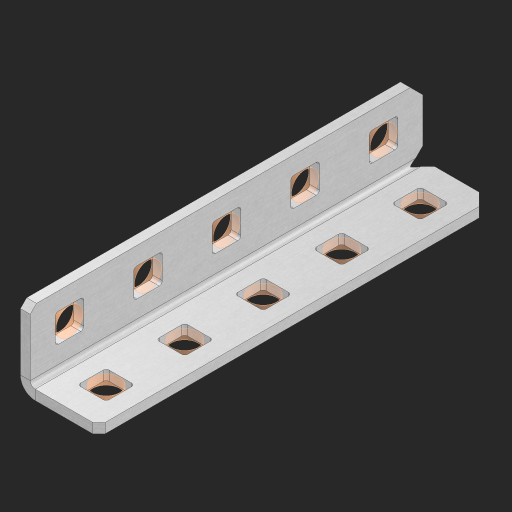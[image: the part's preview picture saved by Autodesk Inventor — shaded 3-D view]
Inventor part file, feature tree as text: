
AUTODESK INVENTOR PART (.ipt)
format: ipt  version: 2023 (Build 270158000, 158)  size: 510,976 bytes
history: native  units: in
note: dims shown in document units (in); Inventor stores cm internally (conversion verified against a paired STEP export)
features: other x16, extrude x11, sheet_metal_op x8, sketch x5, pattern_linear x1, mirror x1, chamfer x1
ambient origin geometry x8: Origin, YZ Plane, XZ Plane, XY Plane, X Axis, Y Axis, Z Axis, Center Point
bodies: Solid1 (feature_tree), Body (feature_tree)
feature tree (43):
  sheet_metal_op  "Flanges"
  sheet_metal_op  "Body Pattern"
  other  "Arc Length"
  pattern_linear  "Notch Pattern"  Spacing1=0.125in  [1 undecoded]
  other  "Diagonal Plane"
  mirror  "Everything Mirrored"
  chamfer  "End Chamfer"
  sketch  "Sketch1"  dims[d0=0.5in]
  other  "Plate1"
  sketch  "Sketch2"  dims[d1=2.5in]
  other  "Plate2"
  sheet_metal_op  "Bend1"
  sheet_metal_op  "Corner1"
  sketch  "Sketch8"  dims[d2=0.0625in]
  sketch  "Sketch9"  dims[d3=0.0625in]
  other  "Srf91"
  sheet_metal_op  "Body Pattern Sketch"
  other  "Srf92"
  sketch  "Sketch13"  dims[d4=0.0312in d5=0.125in d6=0.0625in d7=0.5in d8=90.0deg d9=0.0312in d10=0.25in d11=0.0625in d12=0.0625in d49=0.182in d50=0.02in d52=0.25in d53=0.0625in d54=0.0in d55=0.172in d56=1.0in d57=0.0in d85=0.1473in d86=0.1782in d89=0.0625in d90=0.0in d91=0.04in d92=0.0491in d95=2.5in d96=0.04in d97=0.25in d98=45.0deg d123=0.204in d126=0.0491in d127=0.1473in d128=0.08in d129=0.04in d130=2.5in d131=1.9685in d133=0.5in d134=0.3937in d136=1.0in]
  other  "Srf856"
  other  "Srf857"
  other  "Srf858"
  other  "Srf859"
  other  "Srf1275"
  other  "Srf1276"
  other  "Srf1278"
  other  "Srf1279"
  other  "Srf1280"
  other  "Srf1281"
  sheet_metal_op  "Body Stamp"
  sheet_metal_op  "Body Circle"
  sheet_metal_op  "Notch"
  extrude  "ExtrusionSrf92"  Depth=0.0625in
  extrude  "ExtrusionSrf856"  Depth=0.5in TaperAngle=90.0deg
  extrude  "ExtrusionSrf857"  Depth=0.25in
  extrude  "ExtrusionSrf858"  Depth=0.0625in
  extrude  "ExtrusionSrf859"  Depth=0.0625in
  extrude  "ExtrusionSrf1275"  Depth=0.3937in
  extrude  "ExtrusionSrf1276"  Depth=0.02in
  extrude  "ExtrusionSrf1277"  Depth=0.25in
  extrude  "ExtrusionSrf1278"  Depth=0.0625in
  extrude  "ExtrusionSrf1279"  TaperAngle=0.0deg  [1 undecoded]
  extrude  "ExtrusionSrf1280"  Depth=0.3937in
note: 2 required parameter values undecoded (feature->parameter linkage not recoverable at this tier; creation-order binding heuristic only, values carry confidence <= 0.55)
